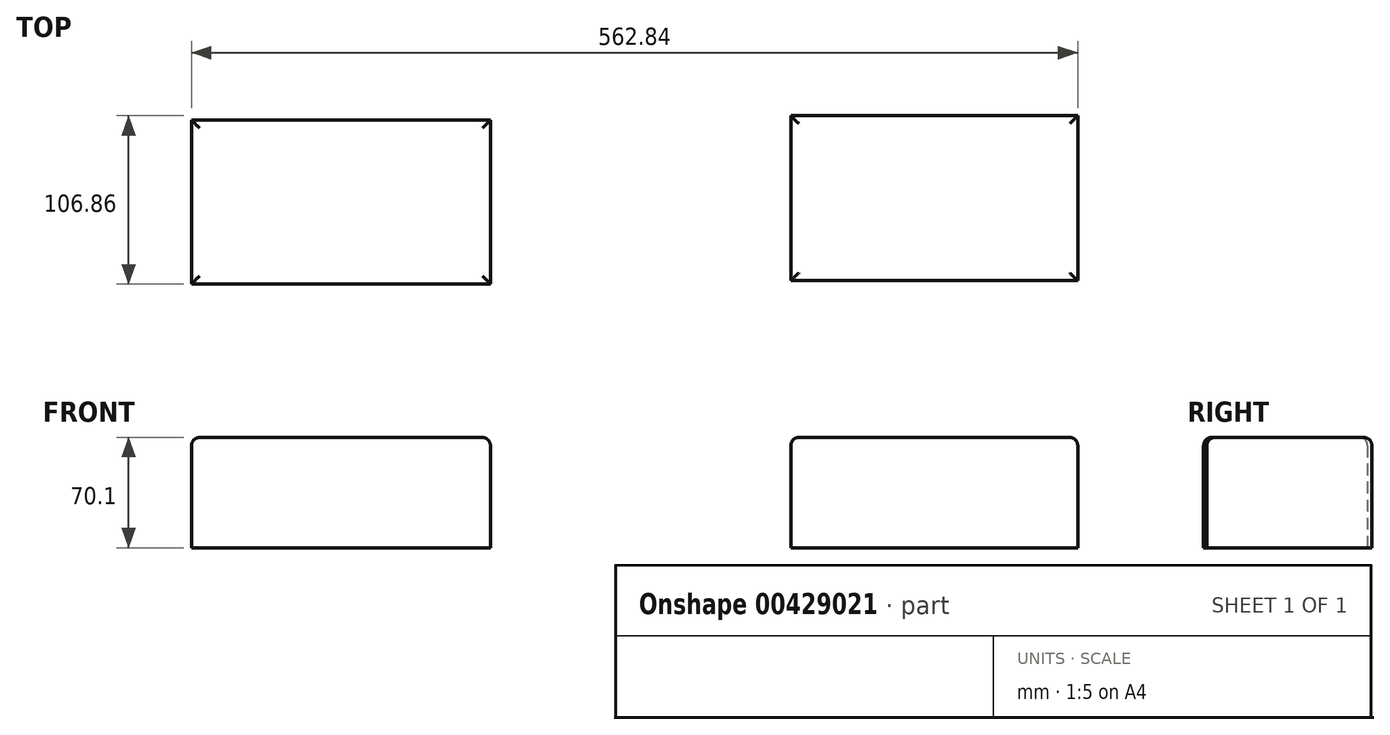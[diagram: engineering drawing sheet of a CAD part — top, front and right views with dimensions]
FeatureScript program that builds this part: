
annotation { "Feature Type Name" : "Feature", "Feature Type Description" : "" }
export const myFeature = defineFeature(function(context is Context, id is Id, definition is map)
    precondition{}
    {
        {
            var Q0;
            Q0=qCreatedBy(makeId("Top.planeOp"),FACE);
            var sketch = newSketch(context, id + "F0", { "sketchPlane" : qUnion([Q0])});
            skLineSegment(sketch, "E0.bottom", {"start": v(-123.53, 31.72) * mm, "end": v(66.32, 31.72) * mm});
            skLineSegment(sketch, "E0.top", {"start": v(-123.53, -72.38) * mm, "end": v(66.32, -72.38) * mm});
            skLineSegment(sketch, "E0.left", {"start": v(-123.53, 31.72) * mm, "end": v(-123.53, -72.38) * mm});
            skLineSegment(sketch, "E0.right", {"start": v(66.32, 31.72) * mm, "end": v(66.32, -72.38) * mm});
            skSolve(sketch);
        }
        {
            var Q0;
            Q0=makeQuery(id+"F0.imprint","IMPRINT",FACE,{"disambiguationData":[TD([[makeQuery(id+"F0.imprint","IMPRINT",EDGE,{"derivedFrom":sQuery(id+"F0.wireOp",EDGE,"E0.bottom")}),-1.0]])]});
            extrude(context, id + "F1", {"entities" : qUnion([Q0]), "depth" : 70.1 * mm});
        }
        {
            var Q0;
            Q0=qCreatedBy(makeId("Top.planeOp"),FACE);
            var sketch = newSketch(context, id + "F2", { "sketchPlane" : qUnion([Q0])});
            skLineSegment(sketch, "E1.bottom", {"start": v(257.08, 34.48) * mm, "end": v(439.31, 34.48) * mm});
            skLineSegment(sketch, "E1.top", {"start": v(257.08, -70.34) * mm, "end": v(439.31, -70.34) * mm});
            skLineSegment(sketch, "E1.left", {"start": v(257.08, 34.48) * mm, "end": v(257.08, -70.34) * mm});
            skLineSegment(sketch, "E1.right", {"start": v(439.31, 34.48) * mm, "end": v(439.31, -70.34) * mm});
            skSolve(sketch);
        }
        {
            var Q0;
            Q0=makeQuery(id+"F2.imprint","IMPRINT",FACE,{"disambiguationData":[TD([[makeQuery(id+"F2.imprint","IMPRINT",EDGE,{"derivedFrom":sQuery(id+"F2.wireOp",EDGE,"E1.bottom")}),-1.0]])]});
            extrude(context, id + "F3", {"entities" : qUnion([Q0]), "depth" : 70.1 * mm});
        }
        {
            var Q0;
            Q0=makeQuery(id+"F1.opExtrude","CAP_EDGE",EDGE,{"disambiguationData":[OSD([sQuery(id+"F0.wireOp",EDGE,"E0.top")])],"isStart":false});
            var Q1;
            Q1=makeQuery(id+"F1.opExtrude","CAP_EDGE",EDGE,{"disambiguationData":[OSD([sQuery(id+"F0.wireOp",EDGE,"E0.right")])],"isStart":false});
            var Q2;
            Q2=makeQuery(id+"F1.opExtrude","CAP_EDGE",EDGE,{"disambiguationData":[OSD([sQuery(id+"F0.wireOp",EDGE,"E0.bottom")])],"isStart":false});
            var Q3;
            Q3=makeQuery(id+"F3.opExtrude","CAP_EDGE",EDGE,{"disambiguationData":[OSD([sQuery(id+"F2.wireOp",EDGE,"E1.left")])],"isStart":false});
            var Q4;
            Q4=makeQuery(id+"F3.opExtrude","CAP_EDGE",EDGE,{"disambiguationData":[OSD([sQuery(id+"F2.wireOp",EDGE,"E1.top")])],"isStart":false});
            var Q5;
            Q5=makeQuery(id+"F3.opExtrude","CAP_EDGE",EDGE,{"disambiguationData":[OSD([sQuery(id+"F2.wireOp",EDGE,"E1.right")])],"isStart":false});
            var Q6;
            Q6=makeQuery(id+"F3.opExtrude","CAP_EDGE",EDGE,{"disambiguationData":[OSD([sQuery(id+"F2.wireOp",EDGE,"E1.bottom")])],"isStart":false});
            var Q7;
            Q7=makeQuery(id+"F1.opExtrude","CAP_EDGE",EDGE,{"disambiguationData":[OSD([sQuery(id+"F0.wireOp",EDGE,"E0.left")])],"isStart":false});
            fillet(context, id + "F4", {"entities" : qUnion([Q0, Q1, Q2, Q3, Q4, Q5, Q6, Q7]), "radius" : 5.08 * mm, "tangentPropagation" : true, "allowEdgeOverflow" : false});
        }
    });
